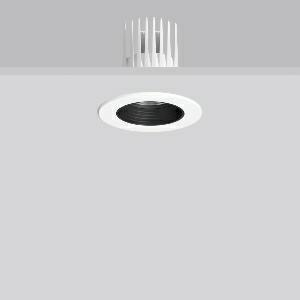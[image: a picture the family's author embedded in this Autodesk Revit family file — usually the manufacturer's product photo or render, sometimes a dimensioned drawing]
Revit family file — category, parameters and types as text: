
# Revit family: heledon_mini_e_901752_002_1_76_473d
name_source: partatom
category: Lighting Fixtures
units: mm (PartAtom-declared; Revit-internal decimal feet)

## family parameters
Cut with Voids When Loaded = No
Host = Face
Light Source = No
Part Type = Normal
Room Calculation Point = No
Round Connector Dimension = Use Diameter
Shared = No

## types (1)
- HELEDON mini E (1 x LED Modul 940, 3200 lm, 4000)
    Apparent Load = 29 VA
    Approval mark = CE
    CIE Flux Codes = 96 100 100 100 100
    Color Rendering = 92
    Color Temperature = 4000
    Default Elevation = 1800 mm
    Description = Series: HELEDON mini
Round recessed downlight. Housing: die-cast aluminium, powder-coated. Black plastic ring and recessed LED to prevent glare from the side. Optical assembly with lens made of plastic (polycarbonate) for the best homogeneous light distribution - can be changed without tools. Best colour rendering index Ra>90. Suitable for Recessed ceiling mounting. Installation without tools thanks to spring fastening system. Including separate LED converter with connecting cable 600 mm.High quality converter without flickering and stroboscopic effect. Through-wiring box (5 pole) available as accessory. The following accessories can be mounted without use of tools: interchangeable lenses, decorative glasses, honeycomb louvre, clear and frosted diffusers, white interchangeable plastic ring. 
Colour: traffic white, matt (RAL 9016)
Diameter: 124 mm
Height: 3 mm
Cut-out diameter: 114 mm
Recess height: 170 mm
Luminaire: recess height: 120 mm
Lamp: LED
Socket: without socket
Colour temperature: 4000K
Colour rendering index (CRI): 92
System power: 29 W
Rated luminous flux: 3200 lm
Luminous efficiency: 110 lm/W
Control gear: Converter, dimmable, DALI
Protection class: II
Type of protection: IP 20
    Height = 0 mm  [stored 0 ft]
    Lamp = 1 x LED Modul 940
    Lamp Light Flux = 3200 lm
    Lamp count = 1
    Length = 124 mm  [stored 0.406824 ft]
    Lifetime = 50000 h
    Luminous efficacy = 110 lm/W
    Manufacturer = RZB
    ModVariant = No
    Model = 901752.002.1.76
    Mounting Place = Ceiling
    Mounting Type = Recessed
    Number of Poles = 1
    OnlyDefault = Yes
    Power Factor = 1
    Product Name = HELEDON mini E
    Product group = Recessed downlights
    ProductGroupID = 402
    Protection Class = Protection class II
    Protection Degree = IP 20
    RLX_Detail_Level = 1
    RLX_Emergency_Light_Flux = 0 lm
    RLX_Emergency_Type = 0
    RLX_Emergency_Type_DB = No
    RlxData = <blob elided: 123841 chars, md5=2a343612>
    Socket = socket
    Standby Power = 0 W
    System Light Flux = 3200 lm
    System Power = 29 W
    Type Comments = Product without accessories
    Type Image = 901656.002.jpg
    URL = http://relux.com
    VarID = ---
    Voltage = 230 V
    Voltage Range = 220-240 V
    Weight = 0.00 kg
    Width = 0 mm  [stored 0 ft]

note: [stored X ft] marks values corroborated as IEEE doubles in the binary element streams (Revit-internal decimal feet)

## geometry (parser evidence)
native form markers: Blend x4, Sweep x13
no freeform markers — native parametric forms only
